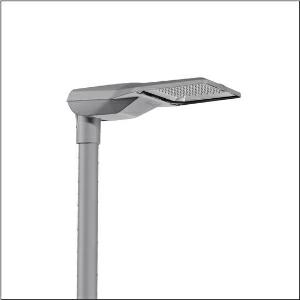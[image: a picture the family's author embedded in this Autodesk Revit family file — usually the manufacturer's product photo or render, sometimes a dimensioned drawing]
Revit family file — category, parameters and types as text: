
# Revit family: streetlight_sl_21_midi___st0_8a_5xe7c63a08nb_ed6b
name_source: partatom
category: Lighting Fixtures
units: mm (PartAtom-declared; Revit-internal decimal feet)

## family parameters
Cut with Voids When Loaded = No
Host = Face
Light Source = No
Part Type = Normal
Room Calculation Point = No
Round Connector Dimension = Use Diameter
Shared = No

## types (1)
- --- (1 x LED, 20350 lm, 151.2 W, 2700K)
    Apparent Load = 151 VA
    CIE Flux Codes = 41 75 97 100 100
    Color Rendering = 70
    Color Temperature = 2700K
    Default Elevation = 1800 mm
    Description = Streetlight SL 21 midi, mast luminaire, primary light control with lens, of PMMA, primary optical cover: cover, of toughened safety glass, transparent, light distribution: ST0.8a, light emission: direct distribution, primary light characteristic: asymmetric, installation type: post-top, side-entry, LED, 3G 1.5mm², High Power LED, rated luminous flux: 20.350lm, luminous efficacy: 135lm/W, light colour: 727, colour temperature: 2700K, control: overheat protection, constant luminous flux control, time-dependent luminous flux control, flexible luminous flux parameterisation, mains connection: 220..240V, AC, 50/60Hz, connection cable pre-assembled, cable length: 12,5m, wiring characteristics: H07RN-F, start of lifetime: 151W, end of service life: 157W, reduction: 70W, luminaire housing, of diecast aluminium, powder-coated, Siteco® metallic grey (DB 702S), corrosivity category C5 mid according to DIN EN ISO 12944, please order mast flange separately, inclination adjustable: 0°, 5°, 10°, 15°, sealing non-destructively replaceable, multi-level sealing system, length: 644mm, width: 335mm, height: 110mm, mast flange for spigot size: 42mm (side-entry): 5XC10008XM4, 60/48mm (side-entry/post-top): 5XC10108XM2, 76/60mm (side-entry/post-top): 5XC10108XM1, protection rating (complete): IP66, insulation class (complete): insulation class II (safety insulation), certification: CE, ENEC, ENEC+, VDE, impact resistance: IK09, permissible operating ambient temperature for outdoor applications: -40..+50°C, standard-compliant lighting for roads and squares, packaging unit: 1 piece

Light Distribution: ST0.8a
    Height = 111 mm
    Lamp = 1 x LED
    Lamp Light Flux = 20350 lm
    Lamp Power = 151.2 W
    Lamp count = 1
    Length = 644 mm
    Luminous efficacy = 135 lm/W
    Manufacturer = Siteco
    ModVariant = No
    Model = 5XE7C63A08NB
    Number of Poles = 1
    OnlyDefault = Yes
    Power Factor = 1
    Product Name = Streetlight SL 21 midi | ST0.8a
    Product group = mast luminaire | pylon top
    ProductGroupID = 6100
    Protection Class = Protection class II
    Protection Degree = IP 66
    RLX_Detail_Level = 1
    RLX_Emergency_Light_Flux = 0 lm
    RLX_Emergency_Type = 0
    RLX_Emergency_Type_DB = No
    RlxData = <blob elided: 90649 chars, md5=c68010d0>
    Socket = socket
    Standby Power = 0 W
    System Light Flux = 20350 lm
    System Power = 151 W
    Type Comments = factory setting: luminous flux: 100 % | Output Level: 100 % | 802 mA
    Type Image = l_1004298.jpg
    URL = http://relux.com
    VarID = @adj_118697
    Voltage = 0 V
    Weight = 0.00 kg
    Width = 336 mm

## geometry (parser evidence)
native form markers: Blend x4, Sweep x11
no freeform markers — native parametric forms only
